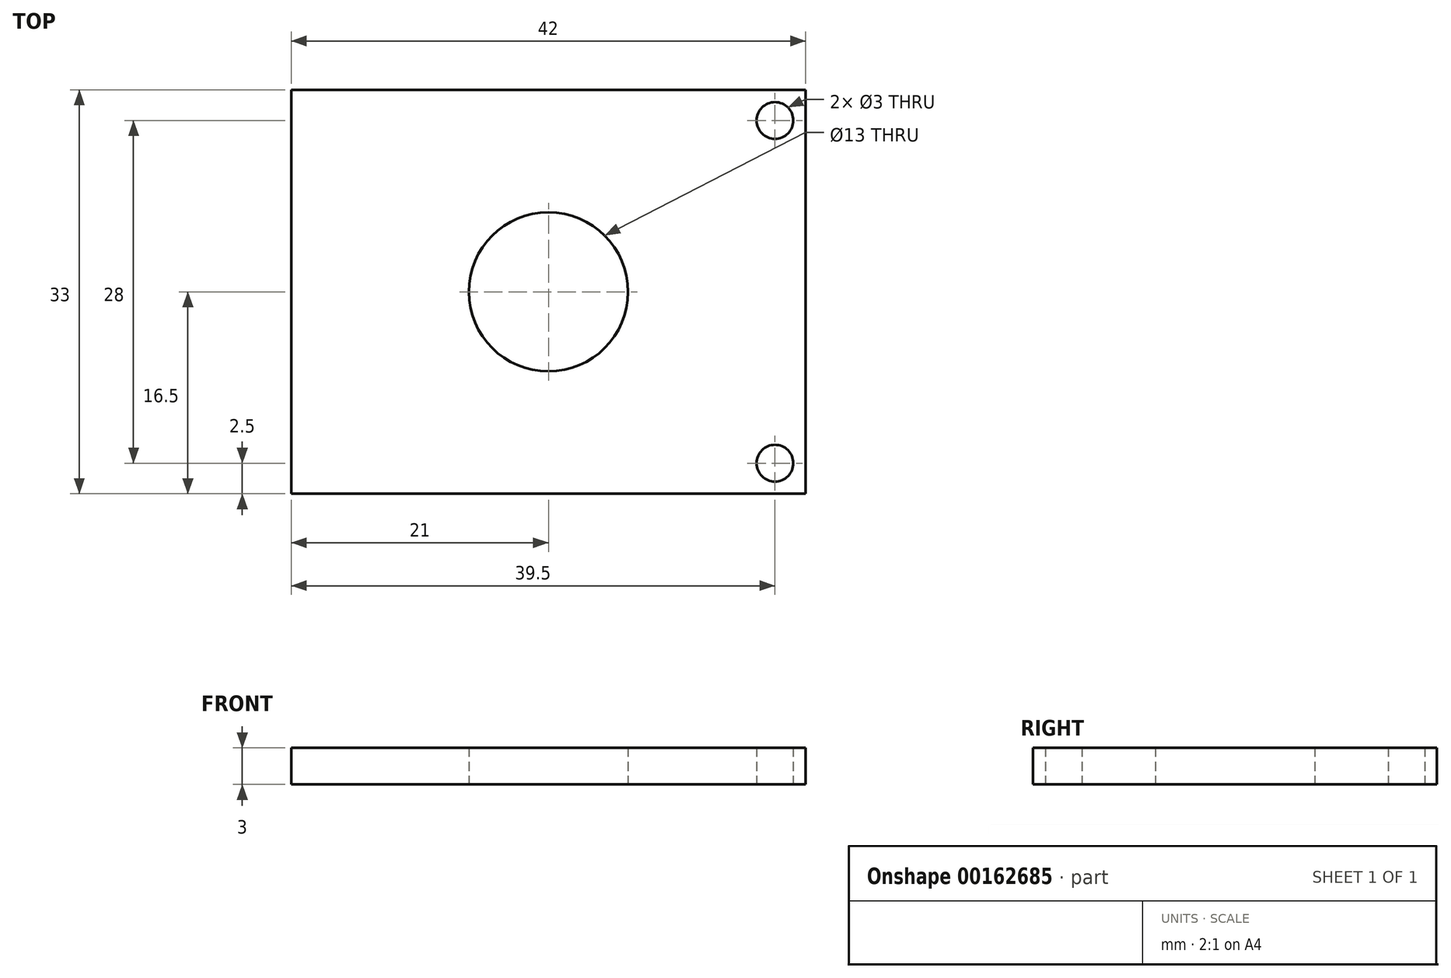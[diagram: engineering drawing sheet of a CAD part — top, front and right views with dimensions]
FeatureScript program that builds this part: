
annotation { "Feature Type Name" : "Feature", "Feature Type Description" : "" }
export const myFeature = defineFeature(function(context is Context, id is Id, definition is map)
    precondition{}
    {
        {
            var Q0;
            Q0=qCreatedBy(makeId("Top.planeOp"),FACE);
            var sketch = newSketch(context, id + "F0", { "sketchPlane" : qUnion([Q0])});
            skLineSegment(sketch, "E0.bottom", {"start": v(21, 16.5) * mm, "end": v(-21, 16.5) * mm});
            skLineSegment(sketch, "E0.top", {"start": v(21, -16.5) * mm, "end": v(-21, -16.5) * mm});
            skLineSegment(sketch, "E0.left", {"start": v(21, 16.5) * mm, "end": v(21, -16.5) * mm});
            skLineSegment(sketch, "E0.right", {"start": v(-21, 16.5) * mm, "end": v(-21, -16.5) * mm});
            skPoint(sketch, "E0.middle", {"position": v(0, 0) * mm});
            skCircle(sketch, "E1", {"center": v(0, 0) * mm, "radius": 6.5 * mm});
            skCircle(sketch, "E2", {"center": v(18.5, 14) * mm, "radius": 1.5 * mm});
            skCircle(sketch, "E3", {"center": v(18.5, -14) * mm, "radius": 1.5 * mm});
            skLineSegment(sketch, "E4", {"start": v(18.5, 14) * mm, "end": v(18.5, 16.5) * mm});
            skLineSegment(sketch, "E5", {"start": v(18.5, 16.5) * mm, "end": v(18.5, 14) * mm});
            skLineSegment(sketch, "E6", {"start": v(18.5, -14) * mm, "end": v(18.5, -16.5) * mm});
            skSolve(sketch);
        }
        {
            var Q0;
            Q0=makeQuery(id+"F0.imprint","IMPRINT",FACE,{"disambiguationData":[TD([[makeQuery(id+"F0.imprint","IMPRINT",EDGE,{"derivedFrom":sQuery(id+"F0.wireOp",EDGE,"E0.bottom")}),1.0]])]});
            extrude(context, id + "F1", {"entities" : qUnion([Q0]), "depth" : 3 * mm});
        }
    });
